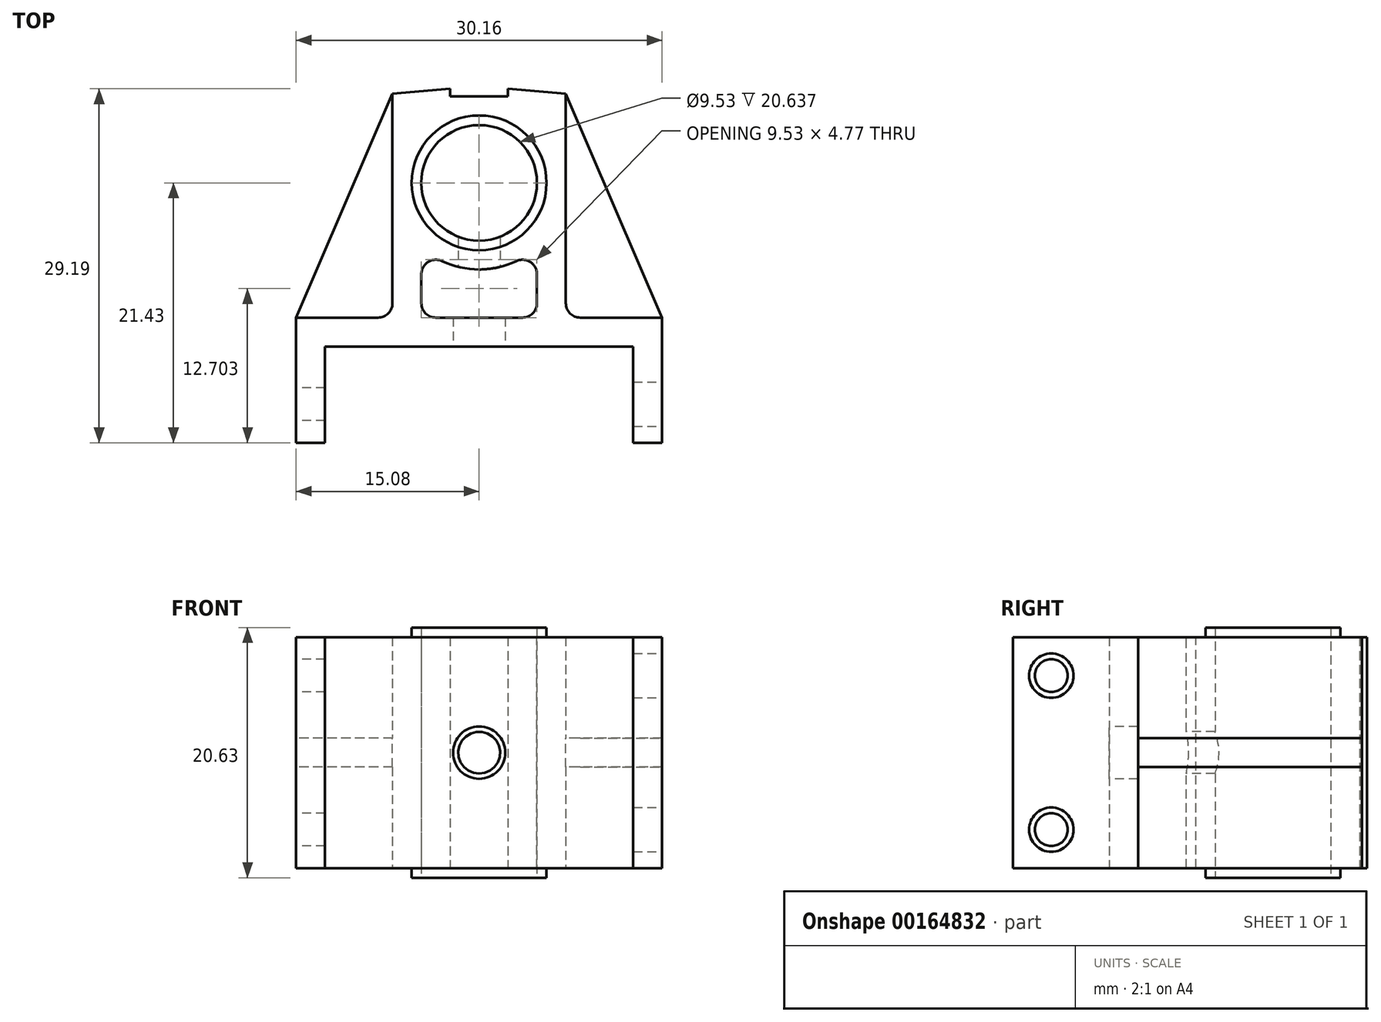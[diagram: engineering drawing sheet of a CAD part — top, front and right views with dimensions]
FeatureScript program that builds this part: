
annotation { "Feature Type Name" : "Feature", "Feature Type Description" : "" }
export const myFeature = defineFeature(function(context is Context, id is Id, definition is map)
    precondition{}
    {
        {
            var Q0;
            Q0=qCreatedBy(makeId("Top.planeOp"),FACE);
            var sketch = newSketch(context, id + "F0", { "sketchPlane" : qUnion([Q0])});
            skCircle(sketch, "E0", {"center": v(0, 0) * mm, "radius": 4.76 * mm});
            skLineSegment(sketch, "E1.bottom", {"start": v(12.7, -21.43) * mm, "end": v(-12.7, -21.43) * mm, "construction": true});
            skLineSegment(sketch, "E1.top", {"start": v(12.7, -13.5) * mm, "end": v(-12.7, -13.5) * mm});
            skLineSegment(sketch, "E1.left", {"start": v(12.7, -21.43) * mm, "end": v(12.7, -13.5) * mm});
            skLineSegment(sketch, "E1.right", {"start": v(-12.7, -21.43) * mm, "end": v(-12.7, -13.5) * mm});
            skLineSegment(sketch, "E2", {"start": v(12.7, -21.43) * mm, "end": v(15.08, -21.43) * mm});
            skLineSegment(sketch, "E3", {"start": v(-12.7, -21.43) * mm, "end": v(-15.08, -21.43) * mm});
            skLineSegment(sketch, "E4", {"start": v(-15.08, -21.43) * mm, "end": v(-15.08, -11.11) * mm});
            skLineSegment(sketch, "E5", {"start": v(15.08, -21.43) * mm, "end": v(15.08, -11.11) * mm});
            skLineSegment(sketch, "E6", {"start": v(-15.08, -11.11) * mm, "end": v(-7.14, -11.11) * mm});
            skLineSegment(sketch, "E7", {"start": v(-7.14, -11.11) * mm, "end": v(-7.14, 7.34) * mm});
            skLineSegment(sketch, "E8", {"start": v(15.08, -11.11) * mm, "end": v(7.14, -11.11) * mm});
            skLineSegment(sketch, "E9", {"start": v(7.14, -11.11) * mm, "end": v(7.14, 7.34) * mm});
            skLineSegment(sketch, "E10", {"start": v(-7.14, -11.11) * mm, "end": v(7.14, -11.11) * mm, "construction": true});
            skLineSegment(sketch, "E11", {"start": v(0, -11.11) * mm, "end": v(0, -13.5) * mm, "construction": true});
            skLineSegment(sketch, "E12", {"start": v(0, 0) * mm, "end": v(0, -11.11) * mm, "construction": true});
            skLineSegment(sketch, "E13", {"start": v(0, 0) * mm, "end": v(0, 7.14) * mm, "construction": true});
            skLineSegment(sketch, "E14", {"start": v(-2.38, 7.14) * mm, "end": v(2.38, 7.14) * mm});
            skLineSegment(sketch, "E15", {"start": v(2.38, 7.14) * mm, "end": v(2.38, 7.76) * mm});
            skLineSegment(sketch, "E16", {"start": v(0, 0) * mm, "end": v(-7.14, 0) * mm, "construction": true});
            skLineSegment(sketch, "E17", {"start": v(2.38, 7.76) * mm, "end": v(7.14, 7.34) * mm});
            skLineSegment(sketch, "E18", {"start": v(-2.38, 7.14) * mm, "end": v(-2.38, 7.76) * mm});
            skLineSegment(sketch, "E19", {"start": v(-2.38, 7.76) * mm, "end": v(-7.14, 7.34) * mm});
            skLineSegment(sketch, "E20", {"start": v(0, 0) * mm, "end": v(0.7, 7.9) * mm, "construction": true});
            skLineSegment(sketch, "E21", {"start": v(0.7, 7.9) * mm, "end": v(2.38, 7.76) * mm, "construction": true});
            skSolve(sketch);
        }
        {
            var Q0;
            Q0=qSketchRegion(id+"F0",true);
            extrude(context, id + "F1", {"entities" : qUnion([Q0]), "depth" : 19.05 * mm});
        }
        {
            var Q0;
            Q0=makeQuery(id+"F1.opExtrude","SWEPT_FACE",FACE,{"disambiguationData":[OSD([sQuery(id+"F0.wireOp",EDGE,"E5")])]});
            var sketch = newSketch(context, id + "F2", { "sketchPlane" : qUnion([Q0])});
            skLineSegment(sketch, "E22.bottom", {"start": v(-21.43, 19.05) * mm, "end": v(-18.26, 19.05) * mm, "construction": true});
            skLineSegment(sketch, "E22.top", {"start": v(-21.43, 15.88) * mm, "end": v(-18.26, 15.88) * mm, "construction": true});
            skLineSegment(sketch, "E22.left", {"start": v(-21.43, 19.05) * mm, "end": v(-21.43, 15.88) * mm, "construction": true});
            skLineSegment(sketch, "E22.right", {"start": v(-18.26, 19.05) * mm, "end": v(-18.26, 15.88) * mm, "construction": true});
            skLineSegment(sketch, "E23.bottom", {"start": v(-21.43, 0) * mm, "end": v(-18.26, 0) * mm, "construction": true});
            skLineSegment(sketch, "E23.top", {"start": v(-21.43, 3.18) * mm, "end": v(-18.26, 3.18) * mm, "construction": true});
            skLineSegment(sketch, "E23.left", {"start": v(-21.43, 0) * mm, "end": v(-21.43, 3.18) * mm, "construction": true});
            skLineSegment(sketch, "E23.right", {"start": v(-18.26, 0) * mm, "end": v(-18.26, 3.18) * mm, "construction": true});
            skCircle(sketch, "E24", {"center": v(-18.26, 15.88) * mm, "radius": 1.83 * mm});
            skCircle(sketch, "E25", {"center": v(-18.26, 3.18) * mm, "radius": 1.83 * mm});
            skSolve(sketch);
        }
        {
            var Q0;
            Q0=qSketchRegion(id+"F2",true);
            var Q1;
            Q1=makeQuery(id+"F1.opExtrude","SWEPT_FACE",FACE,{"disambiguationData":[OSD([sQuery(id+"F0.wireOp",EDGE,"E1.left")])]});
            extrude(context, id + "F3", {"entities" : qUnion([Q0]), "operationType" : NewBodyOperationType.REMOVE, "endBound" : BoundingType.UP_TO_SURFACE, "oppositeDirection" : true, "endBoundEntityFace" : qUnion([Q1]), "depth" : 25.4 * mm});
        }
        {
            var Q0;
            Q0=makeQuery(id+"F1.opExtrude","SWEPT_FACE",FACE,{"disambiguationData":[OSD([sQuery(id+"F0.wireOp",EDGE,"E4")])]});
            var sketch = newSketch(context, id + "F4", { "sketchPlane" : qUnion([Q0])});
            skCircle(sketch, "E26", {"center": v(18.26, 3.18) * mm, "radius": 1.35 * mm});
            skCircle(sketch, "E27", {"center": v(18.26, 15.88) * mm, "radius": 1.35 * mm});
            skSolve(sketch);
        }
        {
            var Q0;
            Q0=qSketchRegion(id+"F4",true);
            var Q1;
            Q1=makeQuery(id+"F1.opExtrude","SWEPT_FACE",FACE,{"disambiguationData":[OSD([sQuery(id+"F0.wireOp",EDGE,"E1.right")])]});
            extrude(context, id + "F5", {"entities" : qUnion([Q0]), "operationType" : NewBodyOperationType.REMOVE, "endBound" : BoundingType.UP_TO_SURFACE, "oppositeDirection" : true, "endBoundEntityFace" : qUnion([Q1]), "depth" : 25.4 * mm});
        }
        {
            var Q0;
            Q0=makeQuery(id+"F1.opExtrude","CAP_FACE",FACE,{"disambiguationData":[OSD([sQuery(id+"F0.wireOp",EDGE,"oFMiMBZJ-tm7e-gSPN-Mg8Y-tAPpBSy2u1vv"),sQuery(id+"F0.wireOp",EDGE,"E0"),sQuery(id+"F0.wireOp",EDGE,"E1.top"),sQuery(id+"F0.wireOp",EDGE,"E1.left"),sQuery(id+"F0.wireOp",EDGE,"E1.right"),sQuery(id+"F0.wireOp",EDGE,"E2"),sQuery(id+"F0.wireOp",EDGE,"E3"),sQuery(id+"F0.wireOp",EDGE,"E4"),sQuery(id+"F0.wireOp",EDGE,"E5"),sQuery(id+"F0.wireOp",EDGE,"E6"),sQuery(id+"F0.wireOp",EDGE,"E7"),sQuery(id+"F0.wireOp",EDGE,"E8"),sQuery(id+"F0.wireOp",EDGE,"E9")])],"isStart":true});
            cPlane(context, id + "F6", {"entities" : qUnion([Q0]), "cplaneType" : CPlaneType.OFFSET, "offset" : 9.52 * mm, "oppositeDirection" : true, "width" : 152.4 * mm, "height" : 152.4 * mm});
        }
        {
            var Q0;
            Q0=qCreatedBy(id+"F6.planeOp",FACE);
            var sketch = newSketch(context, id + "F7", { "sketchPlane" : qUnion([Q0])});
            skLineSegment(sketch, "E28", {"start": v(-7.14, -7.34) * mm, "end": v(-15.08, 11.11) * mm});
            skLineSegment(sketch, "E29", {"start": v(-7.14, 11.11) * mm, "end": v(-7.14, 11.11) * mm});
            skLineSegment(sketch, "E30", {"start": v(-7.14, 11.11) * mm, "end": v(-15.08, 11.11) * mm});
            skLineSegment(sketch, "E31", {"start": v(7.14, 11.11) * mm, "end": v(7.14, 11.11) * mm});
            skLineSegment(sketch, "E32", {"start": v(7.14, 11.11) * mm, "end": v(15.08, 11.11) * mm});
            skLineSegment(sketch, "E33", {"start": v(15.08, 11.11) * mm, "end": v(7.14, -7.34) * mm});
            skLineSegment(sketch, "E34", {"start": v(-7.14, -7.34) * mm, "end": v(-7.14, 11.11) * mm});
            skLineSegment(sketch, "E35", {"start": v(7.14, 11.11) * mm, "end": v(7.14, -7.34) * mm});
            skSolve(sketch);
        }
        {
            var Q0;
            Q0=qSketchRegion(id+"F7",true);
            extrude(context, id + "F8", {"entities" : qUnion([Q0]), "operationType" : NewBodyOperationType.ADD, "endBound" : BoundingType.SYMMETRIC, "depth" : 2.38 * mm});
        }
        {
            var Q0;
            Q0=makeQuery(id+"F1.opExtrude","CAP_FACE",FACE,{"disambiguationData":[OSD([sQuery(id+"F0.wireOp",EDGE,"oFMiMBZJ-tm7e-gSPN-Mg8Y-tAPpBSy2u1vv"),sQuery(id+"F0.wireOp",EDGE,"E0"),sQuery(id+"F0.wireOp",EDGE,"E1.top"),sQuery(id+"F0.wireOp",EDGE,"E1.left"),sQuery(id+"F0.wireOp",EDGE,"E1.right"),sQuery(id+"F0.wireOp",EDGE,"E2"),sQuery(id+"F0.wireOp",EDGE,"E3"),sQuery(id+"F0.wireOp",EDGE,"E4"),sQuery(id+"F0.wireOp",EDGE,"E5"),sQuery(id+"F0.wireOp",EDGE,"E6"),sQuery(id+"F0.wireOp",EDGE,"E7"),sQuery(id+"F0.wireOp",EDGE,"E8"),sQuery(id+"F0.wireOp",EDGE,"E9")])],"isStart":true});
            var sketch = newSketch(context, id + "F9", { "sketchPlane" : qUnion([Q0])});
            skCircle(sketch, "E36", {"center": v(0, 0) * mm, "radius": 4.76 * mm});
            skCircle(sketch, "E37", {"center": v(0, 0) * mm, "radius": 5.56 * mm});
            skSolve(sketch);
        }
        {
            var Q0;
            Q0=makeQuery(id+"F1.opExtrude","CAP_FACE",FACE,{"disambiguationData":[OSD([sQuery(id+"F0.wireOp",EDGE,"oFMiMBZJ-tm7e-gSPN-Mg8Y-tAPpBSy2u1vv"),sQuery(id+"F0.wireOp",EDGE,"E0"),sQuery(id+"F0.wireOp",EDGE,"E1.top"),sQuery(id+"F0.wireOp",EDGE,"E1.left"),sQuery(id+"F0.wireOp",EDGE,"E1.right"),sQuery(id+"F0.wireOp",EDGE,"E2"),sQuery(id+"F0.wireOp",EDGE,"E3"),sQuery(id+"F0.wireOp",EDGE,"E4"),sQuery(id+"F0.wireOp",EDGE,"E5"),sQuery(id+"F0.wireOp",EDGE,"E6"),sQuery(id+"F0.wireOp",EDGE,"E7"),sQuery(id+"F0.wireOp",EDGE,"E8"),sQuery(id+"F0.wireOp",EDGE,"E9")])],"isStart":false});
            cPlane(context, id + "F10", {"entities" : qUnion([Q0]), "cplaneType" : CPlaneType.OFFSET, "offset" : 0.8 * mm, "width" : 152.4 * mm, "height" : 152.4 * mm});
        }
        {
            var Q0;
            Q0=qSketchRegion(id+"F9",true);
            var Q1;
            Q1=qCreatedBy(id+"F10.planeOp",FACE);
            extrude(context, id + "F11", {"entities" : qUnion([Q0]), "operationType" : NewBodyOperationType.ADD, "depth" : 0.8 * mm, "hasSecondDirection" : true, "secondDirectionBound" : SecondDirectionBoundingType.UP_TO_SURFACE, "secondDirectionOppositeDirection" : true, "secondDirectionBoundEntityFace" : qUnion([Q1]), "secondDirectionDepth" : 25.4 * mm});
        }
        {
            var Q0;
            Q0=makeQuery(id+"F1.opExtrude","SWEPT_FACE",FACE,{"disambiguationData":[OSD([sQuery(id+"F0.wireOp",EDGE,"E1.top")])]});
            var sketch = newSketch(context, id + "F12", { "sketchPlane" : qUnion([Q0])});
            skLineSegment(sketch, "E38", {"start": v(0, 19.05) * mm, "end": v(0, 0) * mm, "construction": true});
            skCircle(sketch, "E39", {"center": v(0, 9.53) * mm, "radius": 1.73 * mm});
            skSolve(sketch);
        }
        {
            var Q0;
            Q0=qSketchRegion(id+"F12",true);
            var Q1;
            Q1=makeQuery(id+"F11.boolean.opBoolean","MERGE",FACE,{"derivedFrom":[makeQuery(id+"F1.opExtrude","SWEPT_FACE",FACE,{"disambiguationData":[OSD([sQuery(id+"F0.wireOp",EDGE,"E0")])]}),makeQuery(id+"F11.opExtrude","SWEPT_FACE",FACE,{"disambiguationData":[OSD([sQuery(id+"F9.wireOp",EDGE,"E36")])]})]});
            extrude(context, id + "F13", {"entities" : qUnion([Q0]), "operationType" : NewBodyOperationType.REMOVE, "endBound" : BoundingType.UP_TO_SURFACE, "oppositeDirection" : true, "endBoundEntityFace" : qUnion([Q1]), "depth" : 25.4 * mm});
        }
        {
            var Q0;
            Q0=makeQuery(id+"F1.opExtrude","CAP_FACE",FACE,{"disambiguationData":[OSD([sQuery(id+"F0.wireOp",EDGE,"oFMiMBZJ-tm7e-gSPN-Mg8Y-tAPpBSy2u1vv"),sQuery(id+"F0.wireOp",EDGE,"E0"),sQuery(id+"F0.wireOp",EDGE,"E1.top"),sQuery(id+"F0.wireOp",EDGE,"E1.left"),sQuery(id+"F0.wireOp",EDGE,"E1.right"),sQuery(id+"F0.wireOp",EDGE,"E2"),sQuery(id+"F0.wireOp",EDGE,"E3"),sQuery(id+"F0.wireOp",EDGE,"E4"),sQuery(id+"F0.wireOp",EDGE,"E5"),sQuery(id+"F0.wireOp",EDGE,"E6"),sQuery(id+"F0.wireOp",EDGE,"E7"),sQuery(id+"F0.wireOp",EDGE,"E8"),sQuery(id+"F0.wireOp",EDGE,"E9")])],"isStart":false});
            var sketch = newSketch(context, id + "F14", { "sketchPlane" : qUnion([Q0])});
            skLineSegment(sketch, "E40.bottom", {"start": v(-4.76, -11.11) * mm, "end": v(4.76, -11.11) * mm});
            skLineSegment(sketch, "E40.top", {"start": v(-4.76, -5.32) * mm, "end": v(4.76, -5.32) * mm, "construction": true});
            skLineSegment(sketch, "E40.left", {"start": v(-4.76, -11.11) * mm, "end": v(-4.76, -5.32) * mm});
            skLineSegment(sketch, "E40.right", {"start": v(4.76, -11.11) * mm, "end": v(4.76, -5.32) * mm});
            skLineSegment(sketch, "E41", {"start": v(0, -11.11) * mm, "end": v(0, -13.5) * mm, "construction": true});
            skLineSegment(sketch, "E42", {"start": v(4.76, -11.11) * mm, "end": v(7.14, -11.11) * mm, "construction": true});
            skArc(sketch, "E43", {"start": v(-4.76, -5.32) * mm, "mid": v(0, -7.14) * mm, "end": v(4.76, -5.32) * mm});
            skSolve(sketch);
        }
        {
            var Q0;
            Q0=qSketchRegion(id+"F14",true);
            var Q1;
            Q1=makeQuery(id+"F1.opExtrude","CAP_FACE",FACE,{"disambiguationData":[OSD([sQuery(id+"F0.wireOp",EDGE,"oFMiMBZJ-tm7e-gSPN-Mg8Y-tAPpBSy2u1vv"),sQuery(id+"F0.wireOp",EDGE,"E0"),sQuery(id+"F0.wireOp",EDGE,"E1.top"),sQuery(id+"F0.wireOp",EDGE,"E1.left"),sQuery(id+"F0.wireOp",EDGE,"E1.right"),sQuery(id+"F0.wireOp",EDGE,"E2"),sQuery(id+"F0.wireOp",EDGE,"E3"),sQuery(id+"F0.wireOp",EDGE,"E4"),sQuery(id+"F0.wireOp",EDGE,"E5"),sQuery(id+"F0.wireOp",EDGE,"E6"),sQuery(id+"F0.wireOp",EDGE,"E7"),sQuery(id+"F0.wireOp",EDGE,"E8"),sQuery(id+"F0.wireOp",EDGE,"E9")])],"isStart":true});
            extrude(context, id + "F15", {"entities" : qUnion([Q0]), "operationType" : NewBodyOperationType.REMOVE, "endBound" : BoundingType.UP_TO_SURFACE, "oppositeDirection" : true, "endBoundEntityFace" : qUnion([Q1]), "depth" : 25.4 * mm});
        }
        {
            var Q0;
            Q0=makeQuery(id+"F1.opExtrude","SWEPT_FACE",FACE,{"disambiguationData":[OSD([sQuery(id+"F0.wireOp",EDGE,"E1.top")])]});
            var sketch = newSketch(context, id + "F16", { "sketchPlane" : qUnion([Q0])});
            skCircle(sketch, "E44", {"center": v(0, 9.53) * mm, "radius": 2.15 * mm});
            skSolve(sketch);
        }
        {
            var Q0;
            Q0=qSketchRegion(id+"F16",true);
            var Q1;
            Q1=makeQuery(id+"F15.boolean.opBoolean","COPY",FACE,{"derivedFrom":makeQuery(id+"F15.opExtrude","SWEPT_FACE",FACE,{"disambiguationData":[OSD([sQuery(id+"F14.wireOp",EDGE,"E40.bottom")])]})});
            extrude(context, id + "F17", {"entities" : qUnion([Q0]), "operationType" : NewBodyOperationType.REMOVE, "endBound" : BoundingType.UP_TO_SURFACE, "oppositeDirection" : true, "endBoundEntityFace" : qUnion([Q1]), "depth" : 25.4 * mm});
        }
        {
            var Q0;
            {var subQ0=sQuery(id+"F0.wireOp",EDGE,"E9");var subQ1=sQuery(id+"F0.wireOp",EDGE,"E8");Q0=makeQuery(id+"F8.boolean.opBoolean","SPLIT",EDGE,{"disambiguationData":[TD([makeQuery(id+"F8.opExtrude","CAP_FACE",FACE,{"disambiguationData":[OSD([sQuery(id+"F7.wireOp",EDGE,"kuT9Lr5W-Ujlv-qyoe-8bON-kbdIo9kqYZIf"),sQuery(id+"F7.wireOp",EDGE,"E31"),sQuery(id+"F7.wireOp",EDGE,"E32"),sQuery(id+"F7.wireOp",EDGE,"E33")])],"isStart":true})])],"derivedFrom":makeQuery(id+"F1.opExtrude","SWEPT_EDGE",EDGE,{"disambiguationData":[OSD([subQ1,subQ0])]})});}
            var Q1;
            {var subQ0=sQuery(id+"F0.wireOp",EDGE,"E9");var subQ1=sQuery(id+"F0.wireOp",EDGE,"E8");Q1=makeQuery(id+"F8.boolean.opBoolean","SPLIT",EDGE,{"disambiguationData":[TD([makeQuery(id+"F8.opExtrude","CAP_FACE",FACE,{"disambiguationData":[OSD([sQuery(id+"F7.wireOp",EDGE,"kuT9Lr5W-Ujlv-qyoe-8bON-kbdIo9kqYZIf"),sQuery(id+"F7.wireOp",EDGE,"E31"),sQuery(id+"F7.wireOp",EDGE,"E32"),sQuery(id+"F7.wireOp",EDGE,"E33")])],"isStart":false})])],"derivedFrom":makeQuery(id+"F1.opExtrude","SWEPT_EDGE",EDGE,{"disambiguationData":[OSD([subQ1,subQ0])]})});}
            var Q2;
            {var subQ0=sQuery(id+"F0.wireOp",EDGE,"E7");var subQ1=sQuery(id+"F0.wireOp",EDGE,"E6");Q2=makeQuery(id+"F8.boolean.opBoolean","SPLIT",EDGE,{"disambiguationData":[TD([makeQuery(id+"F8.opExtrude","CAP_FACE",FACE,{"disambiguationData":[OSD([sQuery(id+"F7.wireOp",EDGE,"E28"),sQuery(id+"F7.wireOp",EDGE,"yiKBqqz0-a8bt-GbF6-MsWU-omjT0H6QG2cN"),sQuery(id+"F7.wireOp",EDGE,"E29"),sQuery(id+"F7.wireOp",EDGE,"E30")])],"isStart":true})])],"derivedFrom":makeQuery(id+"F1.opExtrude","SWEPT_EDGE",EDGE,{"disambiguationData":[OSD([subQ1,subQ0])]})});}
            var Q3;
            {var subQ0=sQuery(id+"F0.wireOp",EDGE,"E7");var subQ1=sQuery(id+"F0.wireOp",EDGE,"E6");Q3=makeQuery(id+"F8.boolean.opBoolean","SPLIT",EDGE,{"disambiguationData":[TD([makeQuery(id+"F8.opExtrude","CAP_FACE",FACE,{"disambiguationData":[OSD([sQuery(id+"F7.wireOp",EDGE,"E28"),sQuery(id+"F7.wireOp",EDGE,"yiKBqqz0-a8bt-GbF6-MsWU-omjT0H6QG2cN"),sQuery(id+"F7.wireOp",EDGE,"E29"),sQuery(id+"F7.wireOp",EDGE,"E30")])],"isStart":false})])],"derivedFrom":makeQuery(id+"F1.opExtrude","SWEPT_EDGE",EDGE,{"disambiguationData":[OSD([subQ1,subQ0])]})});}
            var Q4;
            Q4=makeQuery(id+"F15.boolean.opBoolean","COPY",EDGE,{"derivedFrom":makeQuery(id+"F15.opExtrude","SWEPT_EDGE",EDGE,{"disambiguationData":[OSD([sQuery(id+"F14.wireOp",EDGE,"E40.bottom"),sQuery(id+"F14.wireOp",EDGE,"E40.left")])]})});
            var Q5;
            Q5=makeQuery(id+"F15.boolean.opBoolean","COPY",EDGE,{"derivedFrom":makeQuery(id+"F15.opExtrude","SWEPT_EDGE",EDGE,{"disambiguationData":[OSD([sQuery(id+"F14.wireOp",EDGE,"E40.bottom"),sQuery(id+"F14.wireOp",EDGE,"E40.right")])]})});
            var Q6;
            Q6=makeQuery(id+"F15.boolean.opBoolean","COPY",EDGE,{"derivedFrom":makeQuery(id+"F15.opExtrude","SWEPT_EDGE",EDGE,{"disambiguationData":[OSD([sQuery(id+"F14.wireOp",EDGE,"E40.right"),sQuery(id+"F14.wireOp",EDGE,"E43")])]})});
            var Q7;
            Q7=makeQuery(id+"F15.boolean.opBoolean","COPY",EDGE,{"derivedFrom":makeQuery(id+"F15.opExtrude","SWEPT_EDGE",EDGE,{"disambiguationData":[OSD([sQuery(id+"F14.wireOp",EDGE,"E40.left"),sQuery(id+"F14.wireOp",EDGE,"E43")])]})});
            fillet(context, id + "F18", {"entities" : qUnion([Q0, Q1, Q2, Q3, Q4, Q5, Q6, Q7]), "radius" : 1.2 * mm, "tangentPropagation" : true, "allowEdgeOverflow" : false});
        }
    });
